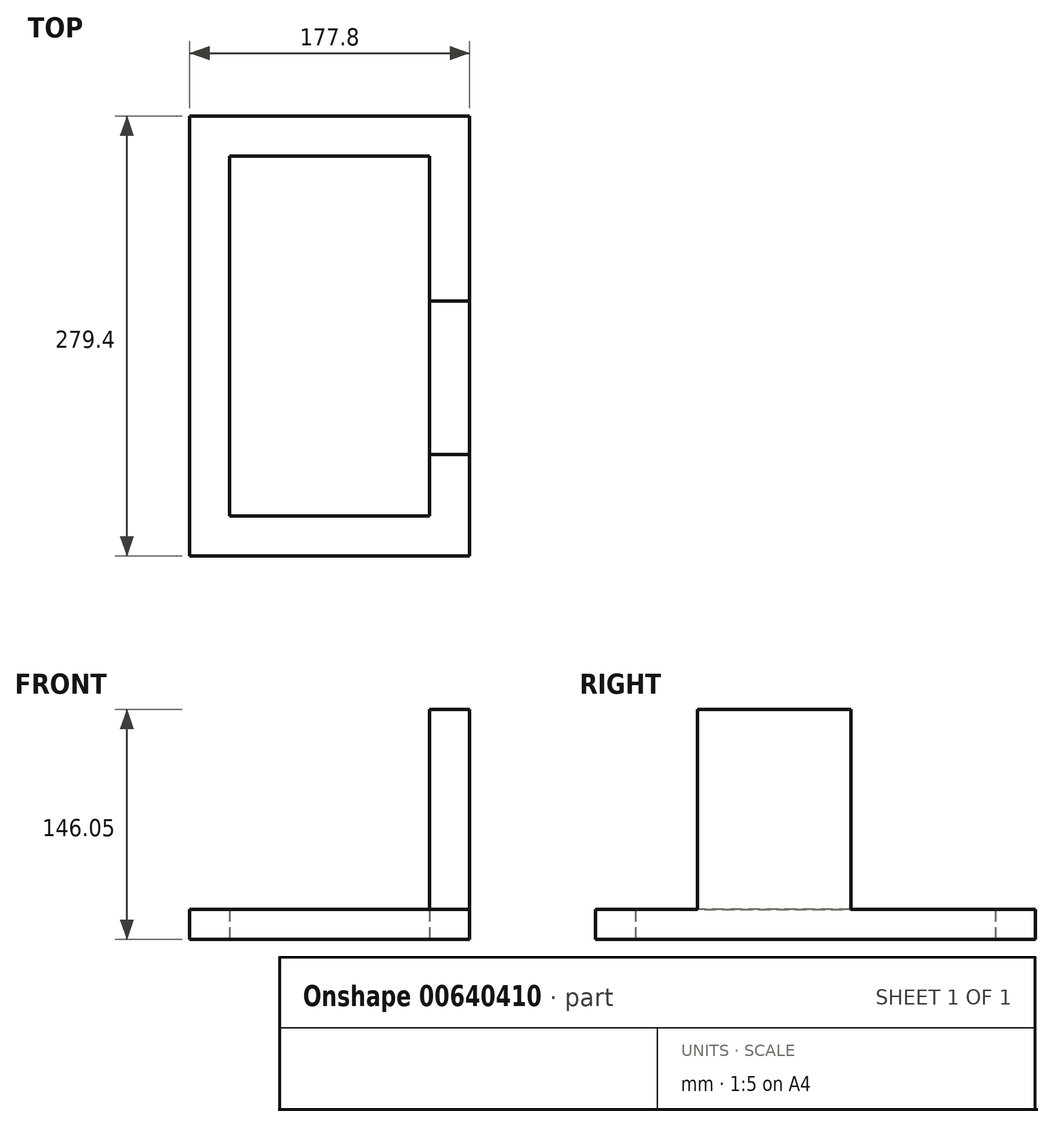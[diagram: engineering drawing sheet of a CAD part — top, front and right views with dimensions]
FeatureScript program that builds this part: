
annotation { "Feature Type Name" : "Feature", "Feature Type Description" : "" }
export const myFeature = defineFeature(function(context is Context, id is Id, definition is map)
    precondition{}
    {
        {
            var Q0;
            Q0=qCreatedBy(makeId("Top.planeOp"),FACE);
            var sketch = newSketch(context, id + "F0", { "sketchPlane" : qUnion([Q0])});
            skLineSegment(sketch, "E0.bottom", {"start": v(0, 0) * mm, "end": v(177.8, 0) * mm});
            skLineSegment(sketch, "E0.top", {"start": v(0, 279.4) * mm, "end": v(177.8, 279.4) * mm});
            skLineSegment(sketch, "E0.left", {"start": v(0, 0) * mm, "end": v(0, 279.4) * mm});
            skLineSegment(sketch, "E0.right", {"start": v(177.8, 0) * mm, "end": v(177.8, 279.4) * mm});
            skSolve(sketch);
        }
        {
            var Q0;
            Q0=makeQuery(id+"F0.imprint","IMPRINT",FACE,{"disambiguationData":[TD([[makeQuery(id+"F0.imprint","IMPRINT",EDGE,{"derivedFrom":sQuery(id+"F0.wireOp",EDGE,"E0.bottom")}),1.0]])]});
            var sketch = newSketch(context, id + "F1", { "sketchPlane" : qUnion([Q0])});
            skLineSegment(sketch, "E1.0.0", {"start": v(177.8, 279.4) * mm, "end": v(0, 279.4) * mm});
            skLineSegment(sketch, "E1.0.1", {"start": v(0, 279.4) * mm, "end": v(0, 0) * mm});
            skLineSegment(sketch, "E1.0.2", {"start": v(0, 0) * mm, "end": v(177.8, 0) * mm});
            skLineSegment(sketch, "E1.0.3", {"start": v(177.8, 0) * mm, "end": v(177.8, 279.4) * mm});
            skLineSegment(sketch, "E2.0", {"start": v(152.4, 254) * mm, "end": v(25.4, 254) * mm});
            skLineSegment(sketch, "E2.1", {"start": v(152.4, 25.4) * mm, "end": v(152.4, 254) * mm});
            skLineSegment(sketch, "E2.2", {"start": v(25.4, 25.4) * mm, "end": v(152.4, 25.4) * mm});
            skLineSegment(sketch, "E2.3", {"start": v(25.4, 254) * mm, "end": v(25.4, 25.4) * mm});
            skSolve(sketch);
        }
        {
            var Q0;
            Q0 = qSketchRegion(id + "F1", true);
            extrude(context, id + "F2", {"entities" : qUnion([Q0]), "depth" : 19.05 * mm, "offsetDistance" : 25.4 * mm});
        }
        {
            var Q0;
            Q0=makeQuery(id+"F2.opExtrude","CAP_FACE",FACE,{"disambiguationData":[OSD([sQuery(id+"F1.wireOp",EDGE,"E1.0.0"),sQuery(id+"F1.wireOp",EDGE,"E1.0.1"),sQuery(id+"F1.wireOp",EDGE,"E1.0.2"),sQuery(id+"F1.wireOp",EDGE,"E1.0.3"),sQuery(id+"F1.wireOp",EDGE,"E2.0"),sQuery(id+"F1.wireOp",EDGE,"E2.1"),sQuery(id+"F1.wireOp",EDGE,"E2.2"),sQuery(id+"F1.wireOp",EDGE,"E2.3")])],"isStart":false});
            var sketch = newSketch(context, id + "F3", { "sketchPlane" : qUnion([Q0])});
            skLineSegment(sketch, "E3.bottom", {"start": v(177.8, 64.48) * mm, "end": v(152.4, 64.48) * mm});
            skLineSegment(sketch, "E3.top", {"start": v(177.8, 161.94) * mm, "end": v(152.4, 161.94) * mm});
            skLineSegment(sketch, "E3.left", {"start": v(177.8, 64.48) * mm, "end": v(177.8, 161.94) * mm});
            skLineSegment(sketch, "E3.right", {"start": v(152.4, 64.48) * mm, "end": v(152.4, 161.94) * mm});
            skSolve(sketch);
        }
        {
            var Q0;
            Q0=makeQuery(id+"F3.imprint","IMPRINT",FACE,{"disambiguationData":[TD([[makeQuery(id+"F3.imprint","IMPRINT",EDGE,{"derivedFrom":sQuery(id+"F3.wireOp",EDGE,"E3.bottom")}),-1.0]])]});
            extrude(context, id + "F4", {"entities" : qUnion([Q0]), "operationType" : NewBodyOperationType.ADD, "depth" : 127 * mm, "offsetDistance" : 25.4 * mm});
        }
    });
